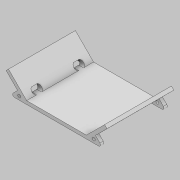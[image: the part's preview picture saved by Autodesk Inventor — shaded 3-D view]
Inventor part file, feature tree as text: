
AUTODESK INVENTOR PART (.ipt)
format: ipt  version: 2022.2 (Build 262287010, 287A)  size: 174,592 bytes
history: native  units: mm
features: extrude x4, sketch x3, other x1, plane x1, mirror x1, fillet x1
ambient origin geometry x8: Origin, YZ Plane, XZ Plane, XY Plane, X Axis, Y Axis, Z Axis, Center Point
bodies: Body1 (feature_tree)
feature tree (11):
  other  "Sólido1"
  extrude  "Extrusión1"  Depth=23.547982mm
  extrude  "Extrusión2"  Depth=3.5mm
  plane  "Plano de trabajo1"
  mirror  "Simetría1"
  extrude  "Extrusión3"  Depth=32.756mm
  fillet  "Empalme1"  Radius=70.0mm
  extrude  "Extrusión4"  Depth=3.5mm TaperAngle=0.0deg
  sketch  "Boceto1"  dims[d0=45.0deg d1=23.547982mm]
  sketch  "Boceto3"  dims[d2=3.5mm d3=3.5mm]
  sketch  "Boceto4"  dims[d4=28.326mm d5=32.756mm d6=70.0mm d7=0.0mm d10=3.5mm d11=0.0mm d12=16.0mm d13=3.0mm d14=7.1mm d15=1.738mm d16=0.0mm d17=0.0mm d18=2.0mm d19=10.0mm d20=5.0mm d21=8.0mm d22=0.0mm d23=0.0mm]
